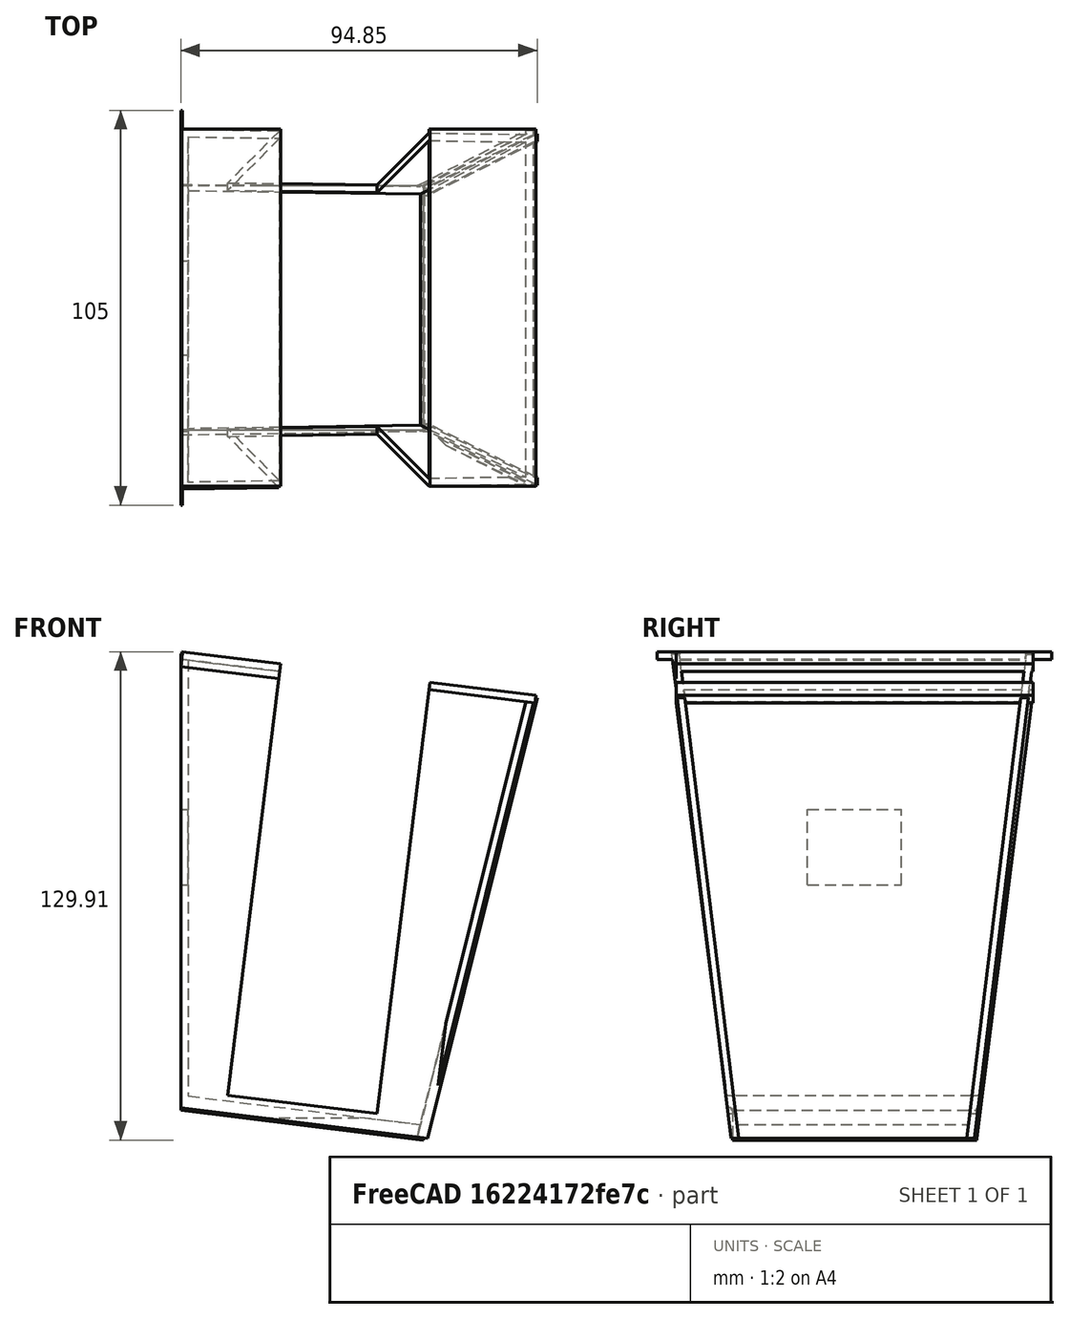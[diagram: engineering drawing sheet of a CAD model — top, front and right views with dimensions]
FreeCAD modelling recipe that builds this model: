
FCSTD DOCUMENT  (FreeCAD 0.16R6706 (Git))
Label: vertical_face_mark1
License: CC-BY 3.0
LicenseURL: http://creativecommons.org/licenses/by/3.0/
objects: Part::Box×20, Part::Cut×14, App::MeasureDistance×3, Part::MultiFuse×2
note: 36 computed .brp shape members not serialized (recipe doc carries the construction recipe); baked Part::Feature solids carry a one-line shape summary decoded from their .brp

FEATURE [Part::Box] Box  label="Cube"
  Height = 120
  Length = 2
  Width = 95
FEATURE [Part::Box] Box001  label="Cube001"
  Height = 140
  Length = 10
  Placement = pos=(0,0,-3) rot=(1,0,0;0.122173rad)
  Width = 15
FEATURE [Part::Box] Box002  label="Cube002"
  Height = 140
  Length = 10
  Placement = pos=(0,80,0) rot=(-1,0,0;0.122173rad)
  Width = 15
FEATURE [Part::Cut] Cut
  Base = -> Box
  Tool = -> Box001
FEATURE [Part::Cut] Cut001
  Base = -> Cut
  Tool = -> Box002
FEATURE [Part::Box] Box003  label="Cube003"
  Height = 20
  Length = 10
  Placement = pos=(0,35,60) rot=(0,0,1;0rad)
  Width = 25
FEATURE [Part::Cut] Cut002
  Base = -> Cut001
  Tool = -> Box003
FEATURE [Part::Box] Box004  label="Cube004"
  Height = 4
  Length = 65
  Placement = pos=(0,15,0) rot=(0,1,0;0.122173rad)
  Width = 65
FEATURE [Part::MultiFuse] Fusion
  Shapes = -> [Cut002,Box004]
FEATURE [App::MeasureDistance] Distance001  label="Distance: 94.724 mm"
  Distance = 94.724
  P1 = (2,0.0101464,120)
  P2 = (2,94.7341,120)
FEATURE [App::MeasureDistance] Distance002  label="Distance: 65 mm"
  Distance = 65
  P1 = (9.92546,15,-1.21869)
  P2 = (9.92546,80,-1.21869)
FEATURE [App::MeasureDistance] Distance003  label="Distance: 120.901 mm"
  Distance = 120.901
  P1 = (0,0.0101464,120)
  P2 = (0,14.7443,0)
FEATURE [Part::Box] Box005  label="Cube005"
  Height = 2
  Length = 95
  Placement = pos=(0,-5,120) rot=(0,1,0;0.122173rad)
  Width = 105
FEATURE [Part::Box] Box006  label="Cube006"
  Height = 140
  Length = 95
  Placement = pos=(0,15,-10) rot=(1,0,0;0.122173rad)
  Width = 2
FEATURE [Part::Box] Box007  label="Cube007"
  Height = 140
  Length = 95
  Placement = pos=(0,77,-10) rot=(-1,0,0;0.122173rad)
  Width = 2
FEATURE [Part::Box] Box008  label="Cube008"
  Height = 120
  Length = 2
  Width = 95
FEATURE [Part::Box] Box009  label="Cube009"
  Height = 140
  Length = 10
  Placement = pos=(0,0,-3) rot=(1,0,0;0.122173rad)
  Width = 15
FEATURE [Part::Box] Box010  label="Cube010"
  Height = 140
  Length = 10
  Placement = pos=(0,80,0) rot=(-1,0,0;0.122173rad)
  Width = 15
FEATURE [Part::Cut] Cut003
  Base = -> Box008
  Tool = -> Box009
FEATURE [Part::Cut] Cut004
  Base = -> Cut003
  Placement = pos=(63,0,-7) rot=(0,1,0;0.244346rad)
  Tool = -> Box010
FEATURE [Part::Box] Box011  label="Cube011"
  Height = 40
  Length = 110
  Placement = pos=(-5,-5,122) rot=(0,1,0;0.122173rad)
  Width = 110
FEATURE [Part::Box] Box012  label="Cube012"
  Height = 40
  Length = 110
  Placement = pos=(-5,-5,122) rot=(0,1,0;0.122173rad)
  Width = 110
FEATURE [Part::Cut] Cut005
  Base = -> Box007
  Tool = -> Box011
FEATURE [Part::Cut] Cut006
  Base = -> Box006
  Tool = -> Box012
FEATURE [Part::Box] Box013  label="Cube013"
  Height = 140
  Length = 40
  Placement = pos=(65,0,-10) rot=(0,1,0;0.244346rad)
  Width = 140
FEATURE [Part::Box] Box014  label="Cube014"
  Height = 140
  Length = 40
  Placement = pos=(65,0,-10) rot=(0,1,0;0.244346rad)
  Width = 140
FEATURE [Part::Cut] Cut007
  Base = -> Cut006
  Tool = -> Box013
FEATURE [Part::Cut] Cut008
  Base = -> Cut005
  Tool = -> Box014
FEATURE [Part::Box] Box015  label="Cube015"
  Height = 20
  Length = 70
  Placement = pos=(-4,0,-19) rot=(0,1,0;0.122173rad)
  Width = 100
FEATURE [Part::Box] Box016  label="Cube016"
  Height = 20
  Length = 70
  Placement = pos=(-4,0,-19) rot=(0,1,0;0.122173rad)
  Width = 100
FEATURE [Part::Cut] Cut009
  Base = -> Cut007
  Tool = -> Box015
FEATURE [Part::Cut] Cut010
  Base = -> Cut008
  Tool = -> Box016
FEATURE [Part::Box] Box017  label="Cube017"
  Height = 140
  Length = 40
  Placement = pos=(12.5,-10,4) rot=(0,1,0;0.122173rad)
  Width = 140
FEATURE [Part::MultiFuse] Fusion001
  Shapes = -> [Cut010,Box005,Fusion,Cut004,Cut009]
FEATURE [Part::Cut] Cut011
  Base = -> Fusion001
  Tool = -> Box017
FEATURE [Part::Box] Box018  label="Cube018"
  Height = 10
  Length = 95
  Placement = pos=(0,-5,118) rot=(0,1,0;0.122173rad)
  Width = 5
FEATURE [Part::Box] Box019  label="Cube019"
  Height = 10
  Length = 95
  Placement = pos=(0,95,118) rot=(0,1,0;0.122173rad)
  Width = 15
FEATURE [Part::Cut] Cut012
  Base = -> Cut011
  Tool = -> Box019
FEATURE [Part::Cut] Cut013
  Base = -> Cut012
  Tool = -> Box018
